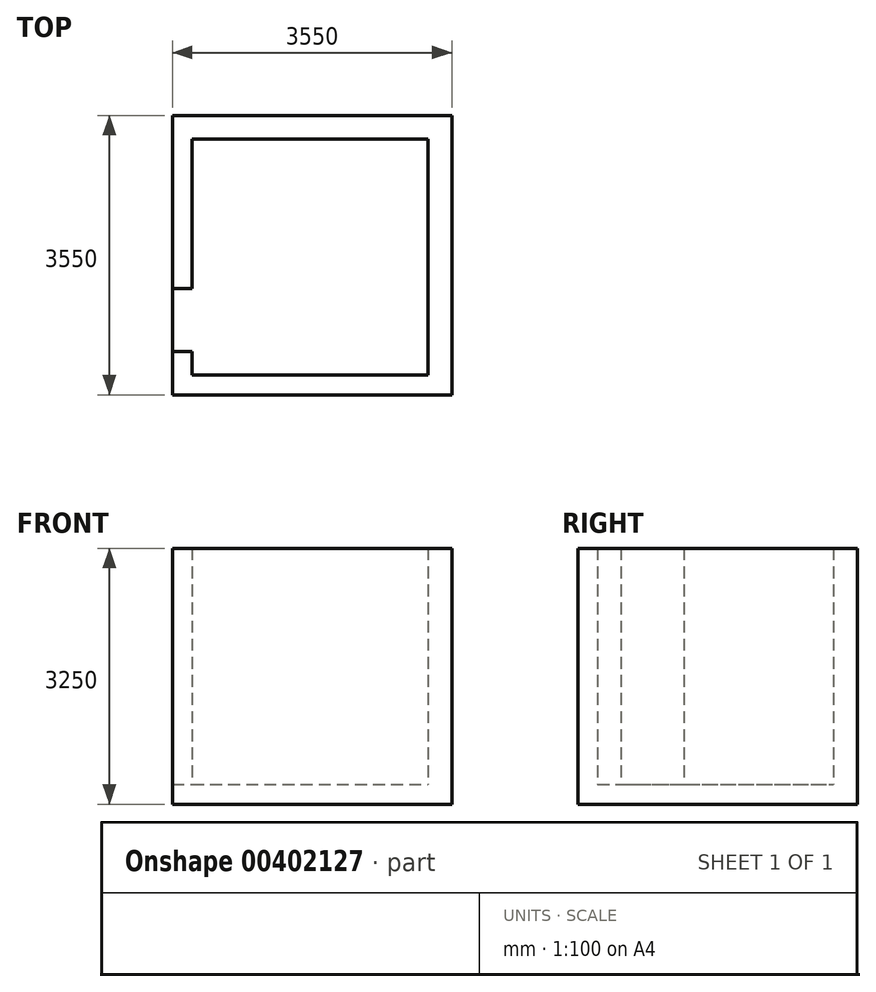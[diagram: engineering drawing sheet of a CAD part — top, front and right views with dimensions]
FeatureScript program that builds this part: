
annotation { "Feature Type Name" : "Feature", "Feature Type Description" : "" }
export const myFeature = defineFeature(function(context is Context, id is Id, definition is map)
    precondition{}
    {
        {
            var Q0;
            Q0=qCreatedBy(makeId("Top.planeOp"),FACE);
            var sketch = newSketch(context, id + "F0", { "sketchPlane" : qUnion([Q0])});
            skLineSegment(sketch, "E0.bottom", {"start": v(0, 0) * mm, "end": v(3000, 0) * mm});
            skLineSegment(sketch, "E0.top", {"start": v(0, 3000) * mm, "end": v(3000, 3000) * mm});
            skLineSegment(sketch, "E0.left", {"start": v(0, 0) * mm, "end": v(0, 300) * mm});
            skLineSegment(sketch, "E0.right", {"start": v(3000, 0) * mm, "end": v(3000, 3000) * mm});
            skLineSegment(sketch, "E1.bottom", {"start": v(-250, 3300) * mm, "end": v(3300, 3300) * mm});
            skLineSegment(sketch, "E1.top", {"start": v(-250, -250) * mm, "end": v(3300, -250) * mm});
            skLineSegment(sketch, "E1.left", {"start": v(-250, 3300) * mm, "end": v(-250, 1100) * mm});
            skLineSegment(sketch, "E1.right", {"start": v(3300, 3300) * mm, "end": v(3300, -250) * mm});
            skLineSegment(sketch, "E2", {"start": v(-250, 1100) * mm, "end": v(0, 1100) * mm});
            skLineSegment(sketch, "E3", {"start": v(-250, 300) * mm, "end": v(0, 300) * mm});
            skLineSegment(sketch, "E4.trimOffspring", {"start": v(-250, 300) * mm, "end": v(-250, -250) * mm});
            skLineSegment(sketch, "E5.trimOffspring", {"start": v(0, 1100) * mm, "end": v(0, 3000) * mm});
            skSolve(sketch);
        }
        {
            var Q0;
            Q0 = qSketchRegion(id + "FPJMj678Sb89mUx_0", true);
            var Q1;
            Q1=makeQuery(id+"F0.imprint","IMPRINT",FACE,{"disambiguationData":[TD([[makeQuery(id+"F0.imprint","IMPRINT",EDGE,{"derivedFrom":sQuery(id+"F0.wireOp",EDGE,"E0.bottom")}),1.0]])]});
            var Q2;
            Q2=makeQuery(id+"F0.imprint","IMPRINT",FACE,{"disambiguationData":[TD([[makeQuery(id+"F0.imprint","IMPRINT",EDGE,{"derivedFrom":sQuery(id+"F0.wireOp",EDGE,"E0.bottom")}),-1.0]])]});
            var Q3;
            Q3=sQuery(id+"F0.wireOp",EDGE,"E0.bottom");
            var Q4;
            Q4=sQuery(id+"F0.wireOp",EDGE,"E0.right");
            var Q5;
            Q5=sQuery(id+"F0.wireOp",EDGE,"E0.left");
            var Q6;
            Q6=sQuery(id+"F0.wireOp",EDGE,"E0.top");
            extrude(context, id + "F1", {"entities" : qUnion([Q0, Q1, Q2]), "surfaceEntities" : qUnion([Q3, Q4, Q5, Q6]), "depth" : 3000 * mm});
        }
        {
            var Q0;
            Q0=qCreatedBy(makeId("Top.planeOp"),FACE);
            var sketch = newSketch(context, id + "F2", { "sketchPlane" : qUnion([Q0])});
            skLineSegment(sketch, "E6.bottom", {"start": v(-250, -250) * mm, "end": v(3300, -250) * mm});
            skLineSegment(sketch, "E6.top", {"start": v(-250, 3300) * mm, "end": v(3300, 3300) * mm});
            skLineSegment(sketch, "E6.left", {"start": v(-250, -250) * mm, "end": v(-250, 3300) * mm});
            skLineSegment(sketch, "E6.right", {"start": v(3300, -250) * mm, "end": v(3300, 3300) * mm});
            skSolve(sketch);
        }
        {
            var Q0;
            Q0=makeQuery(id+"F2.imprint","IMPRINT",FACE,{"disambiguationData":[TD([[makeQuery(id+"F2.imprint","IMPRINT",EDGE,{"derivedFrom":sQuery(id+"F2.wireOp",EDGE,"E6.bottom")}),1.0]])]});
            extrude(context, id + "F3", {"entities" : qUnion([Q0]), "operationType" : NewBodyOperationType.ADD, "oppositeDirection" : true, "depth" : 250 * mm});
        }
    });
